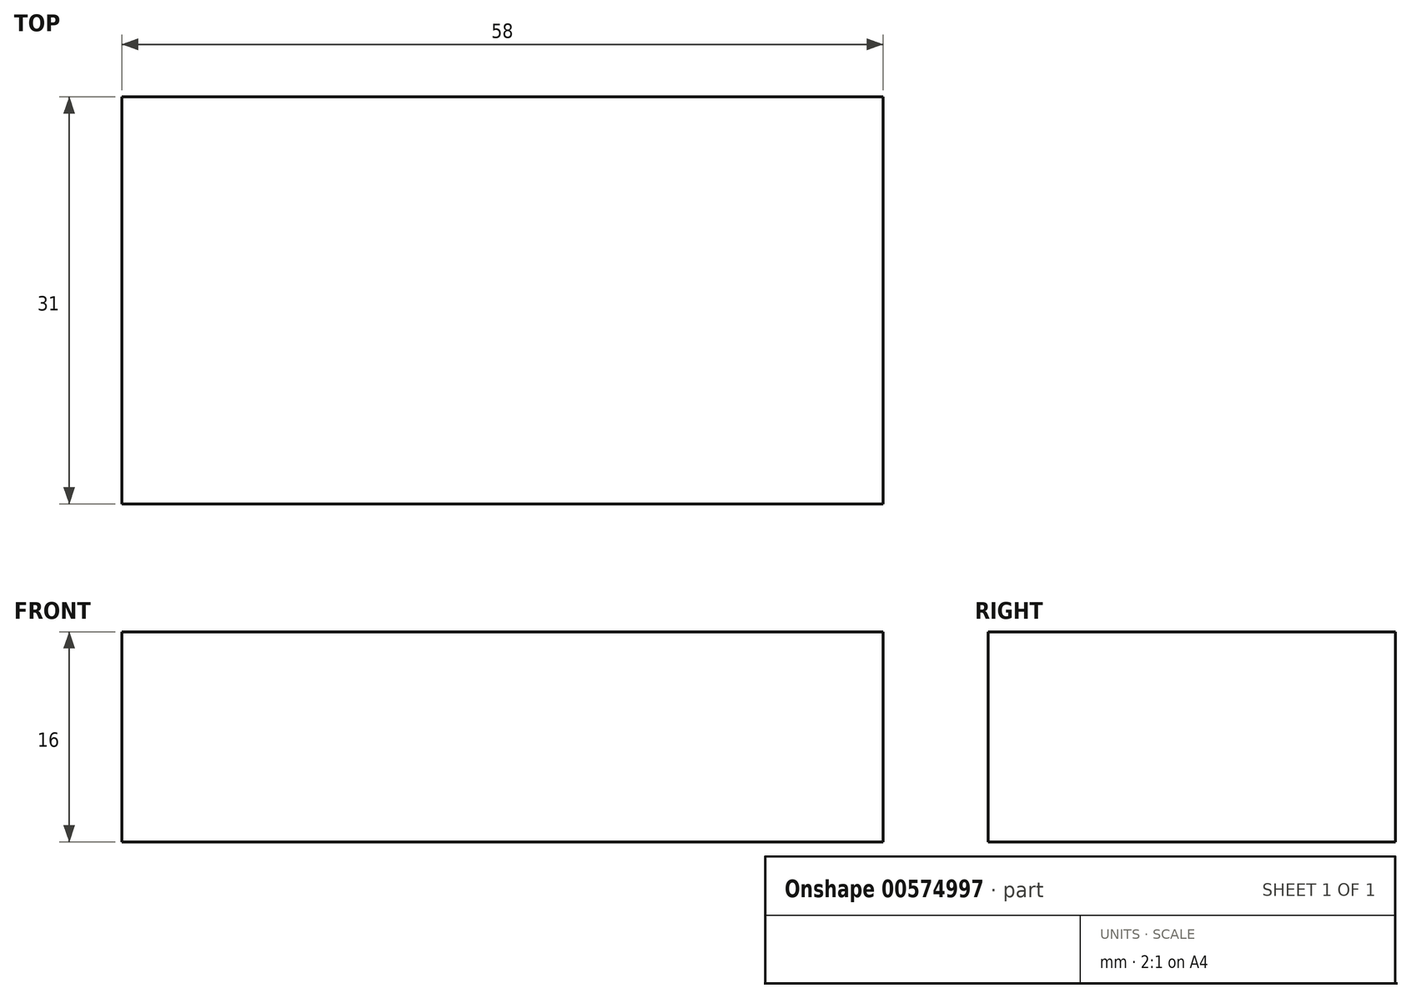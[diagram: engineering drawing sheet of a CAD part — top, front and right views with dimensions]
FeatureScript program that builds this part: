
annotation { "Feature Type Name" : "Feature", "Feature Type Description" : "" }
export const myFeature = defineFeature(function(context is Context, id is Id, definition is map)
    precondition{}
    {
        {
            var Q0;
            Q0=qCreatedBy(makeId("Top.planeOp"),FACE);
            var sketch = newSketch(context, id + "F0", { "sketchPlane" : qUnion([Q0])});
            skLineSegment(sketch, "E0.bottom", {"start": v(-29, 15.5) * mm, "end": v(29, 15.5) * mm});
            skLineSegment(sketch, "E0.top", {"start": v(-29, -15.5) * mm, "end": v(29, -15.5) * mm});
            skLineSegment(sketch, "E0.left", {"start": v(-29, 15.5) * mm, "end": v(-29, -15.5) * mm});
            skLineSegment(sketch, "E0.right", {"start": v(29, 15.5) * mm, "end": v(29, -15.5) * mm});
            skPoint(sketch, "E0.middle", {"position": v(0, 0) * mm});
            skSolve(sketch);
        }
        {
            var Q0;
            Q0 = qSketchRegion(id + "F0", true);
            extrude(context, id + "F1", {"entities" : qUnion([Q0]), "depth" : 8 * mm, "offsetDistance" : 25 * mm, "hasSecondDirection" : true, "secondDirectionOppositeDirection" : true, "secondDirectionDepth" : 8 * mm});
        }
    });
